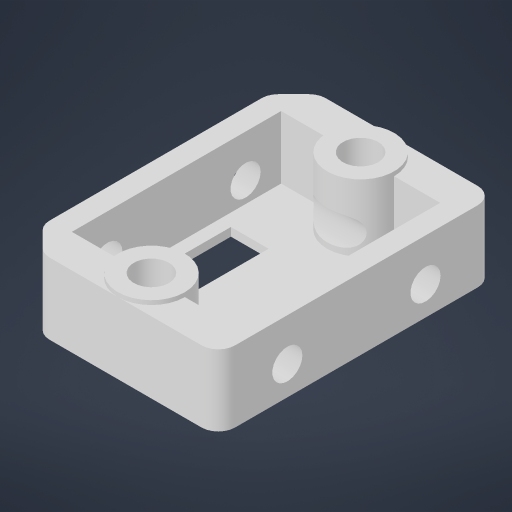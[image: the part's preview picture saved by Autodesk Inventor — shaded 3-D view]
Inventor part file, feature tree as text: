
AUTODESK INVENTOR PART (.ipt)
format: ipt  version: 2024.1 (Build 281209000, 209)  size: 332,288 bytes
history: native  units: mm
features: extrude x10, sketch x8, projected_geometry x4, plane x2, chamfer x1, fillet x1
ambient origin geometry x8: Origin, YZ Plane, XZ Plane, XY Plane, X Axis, Y Axis, Z Axis, Center Point
bodies: Solid1 (feature_tree)
feature tree (26):
  extrude  "Extrusion1"  Depth=20.0mm
  extrude  "Extrusion2"  Depth=25.0mm
  extrude  "Extrusion3"  Depth=4.0mm
  sketch  "Sketch4"  dims[d7=5.0mm d9=10.0mm]
  extrude  "Extrusion5"  Depth=10.0mm
  sketch  "Sketch6"  dims[d12=1.0mm d13=0.0mm d14=8.0mm d15=0.0mm]
  plane  "Work Plane1"
  extrude  "Extrusion6"  Depth=8.0mm TaperAngle=0.0deg
  plane  "Work Plane2"
  extrude  "Extrusion7"  Depth=1.0mm
  extrude  "Extrusion8"  Depth=7.5mm TaperAngle=0.0deg
  extrude  "Extrusion9"  Depth=2.0mm
  chamfer  "Chamfer1"  Distance=10.0mm
  extrude  "Extrusion10"  Depth=2.0mm TaperAngle=0.0deg
  extrude  "Extrusion11"  Depth=2.0mm TaperAngle=0.0deg
  fillet  "Fillet1"  Radius=10.0mm
  sketch  "Sketch1"  dims[d0=15.0mm d1=20.0mm]
  sketch  "Sketch2"  dims[d2=4.2mm d3=25.0mm]
  projected_geometry  "Projected Loop1"
  sketch  "Sketch3"  dims[d4=5.0mm d6=4.0mm]
  projected_geometry  "Projected Loop2"
  sketch  "Sketch8"  dims[d16=4.5mm d17=1.0mm]
  sketch  "Sketch9"  dims[d18=1.5mm d21=7.5mm d22=0.0mm]
  projected_geometry  "Projected Loop3"
  sketch  "Sketch10"  dims[d23=3.6mm d24=16.51mm d28=10.0mm d29=0.0mm d31=2.25mm d32=0.0mm d33=5.25mm d34=0.0mm d35=10.0mm d36=0.0mm d37=33.5mm d38=0.0mm d39=6.0mm d40=2.0mm d41=45.0deg d42=3.0mm d43=0.0mm d44=3.0mm d45=0.0mm d46=2.0mm d26=0.5mm d27=0.872665mm]
  projected_geometry  "Projected Loop4"
